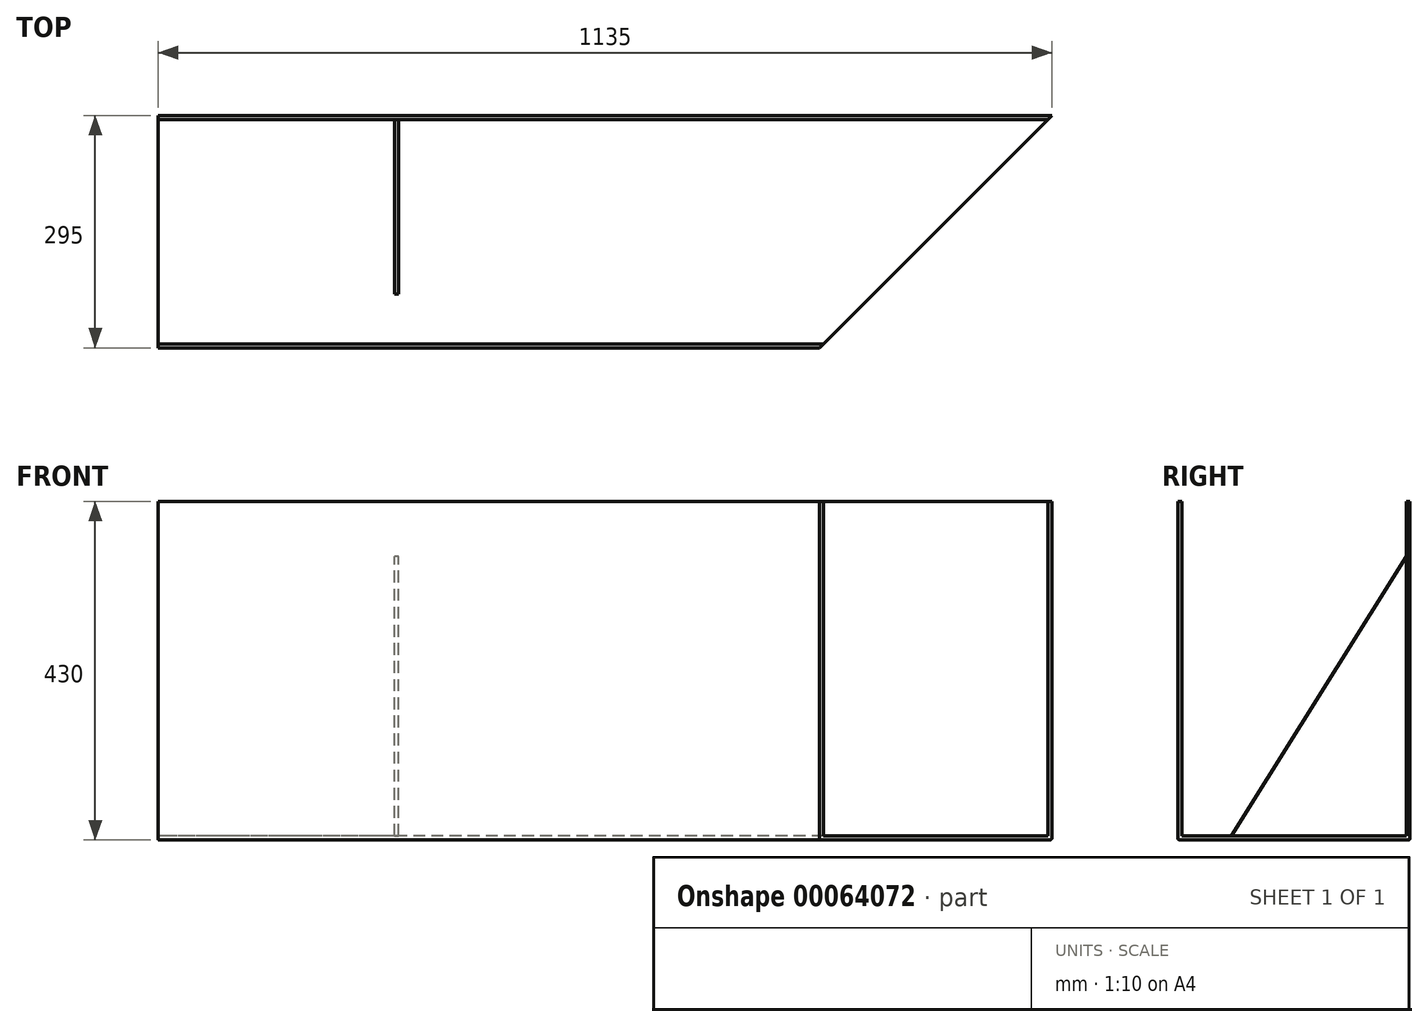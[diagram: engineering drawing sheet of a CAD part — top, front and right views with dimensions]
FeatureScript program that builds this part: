
annotation { "Feature Type Name" : "Feature", "Feature Type Description" : "" }
export const myFeature = defineFeature(function(context is Context, id is Id, definition is map)
    precondition{}
    {
        {
            var Q0;
            Q0=qCreatedBy(makeId("Right.planeOp"),FACE);
            var sketch = newSketch(context, id + "F0", { "sketchPlane" : qUnion([Q0])});
            skLineSegment(sketch, "E0.left", {"start": v(0, 0) * mm, "end": v(0, 430) * mm});
            skLineSegment(sketch, "E1", {"start": v(0, 0) * mm, "end": v(-295, 0) * mm});
            skLineSegment(sketch, "E2", {"start": v(-295, 0) * mm, "end": v(-295, 430) * mm});
            skLineSegment(sketch, "E3.0", {"start": v(-290, 5) * mm, "end": v(-290, 430) * mm});
            skLineSegment(sketch, "E3.1", {"start": v(-5, 5) * mm, "end": v(-290, 5) * mm});
            skLineSegment(sketch, "E3.2", {"start": v(-5, 5) * mm, "end": v(-5, 430) * mm});
            skLineSegment(sketch, "E4", {"start": v(0, 430) * mm, "end": v(-5, 430) * mm});
            skLineSegment(sketch, "E5", {"start": v(-290, 430) * mm, "end": v(-295, 430) * mm});
            skSolve(sketch);
        }
        {
            var Q0;
            Q0=makeQuery(id+"F0.imprint","IMPRINT",FACE,{"disambiguationData":[TD([[makeQuery(id+"F0.imprint","IMPRINT",EDGE,{"derivedFrom":sQuery(id+"F0.wireOp",EDGE,"E0.bottom")}),-1.0]])]});
            var Q1;
            Q1=makeQuery(id+"F0.imprint","IMPRINT",FACE,{"disambiguationData":[TD([[makeQuery(id+"F0.imprint","IMPRINT",EDGE,{"derivedFrom":sQuery(id+"F0.wireOp",EDGE,"E0.left")}),1.0]])]});
            extrude(context, id + "F1", {"entities" : qUnion([Q0, Q1]), "depth" : 1200 * mm});
        }
        {
            var Q0;
            Q0=qCreatedBy(makeId("Right.planeOp"),FACE);
            cPlane(context, id + "F2", {"entities" : qUnion([Q0]), "cplaneType" : CPlaneType.OFFSET, "offset" : 300 * mm, "width" : 150 * mm, "height" : 150 * mm});
        }
        {
            var Q0;
            Q0=qCreatedBy(id+"F2.planeOp",FACE);
            var sketch = newSketch(context, id + "F3", { "sketchPlane" : qUnion([Q0])});
            skLineSegment(sketch, "E6.0", {"start": v(-5, 0) * mm, "end": v(-5, 360) * mm});
            skLineSegment(sketch, "E7.0", {"start": v(-5, 0) * mm, "end": v(-230, 0) * mm});
            skPoint(sketch, "E8", {"position": v(-230, 0) * mm});
            skPoint(sketch, "E9", {"position": v(-5, 360) * mm});
            skLineSegment(sketch, "E10", {"start": v(-5, 360) * mm, "end": v(-230, 0) * mm});
            skSolve(sketch);
        }
        {
            var Q0;
            Q0=makeQuery(id+"F3.imprint","IMPRINT",FACE,{"disambiguationData":[TD([[makeQuery(id+"F3.imprint","IMPRINT",EDGE,{"derivedFrom":sQuery(id+"F3.wireOp",EDGE,"E6.0")}),1.0]])]});
            extrude(context, id + "F4", {"entities" : qUnion([Q0]), "depth" : 5 * mm});
        }
        {
            var Q0;
            Q0=qCreatedBy(makeId("Top.planeOp"),FACE);
            var sketch = newSketch(context, id + "F5", { "sketchPlane" : qUnion([Q0])});
            skLineSegment(sketch, "E11.bottom", {"start": v(0, 0) * mm, "end": v(1200, 0) * mm});
            skLineSegment(sketch, "E11.top", {"start": v(0, -230) * mm, "end": v(1200, -230) * mm});
            skLineSegment(sketch, "E11.left", {"start": v(0, 0) * mm, "end": v(0, -230) * mm});
            skLineSegment(sketch, "E11.right", {"start": v(1200, 0) * mm, "end": v(1200, -230) * mm});
            skSolve(sketch);
        }
        {
            var Q0;
            Q0=makeQuery(id+"F5.imprint","IMPRINT",FACE,{"disambiguationData":[TD([[makeQuery(id+"F5.imprint","IMPRINT",EDGE,{"derivedFrom":sQuery(id+"F5.wireOp",EDGE,"E11.bottom")}),-1.0]])]});
            extrude(context, id + "F6", {"entities" : qUnion([Q0]), "operationType" : NewBodyOperationType.ADD, "depth" : 4 * mm});
        }
        {
            var Q0;
            Q0=makeQuery(id+"F1.opExtrude","SWEPT_EDGE",EDGE,{"disambiguationData":[OSD([sQuery(id+"F0.wireOp",EDGE,"E0.left"),sQuery(id+"F0.wireOp",EDGE,"E1")])]});
            var Q1;
            Q1=makeQuery(id+"F1.opExtrude","SWEPT_EDGE",EDGE,{"disambiguationData":[OSD([sQuery(id+"F0.wireOp",EDGE,"E1"),sQuery(id+"F0.wireOp",EDGE,"E2")])]});
            fillet(context, id + "F7", {"entities" : qUnion([Q0, Q1]), "radius" : 2 * mm, "tangentPropagation" : true, "allowEdgeOverflow" : false});
        }
        {
            var Q0;
            Q0=makeQuery(id+"F1.opExtrude","SWEPT_FACE",FACE,{"disambiguationData":[OSD([sQuery(id+"F0.wireOp",EDGE,"E4")])]});
            var sketch = newSketch(context, id + "F8", { "sketchPlane" : qUnion([Q0])});
            skLineSegment(sketch, "E12.top", {"start": v(0, -295) * mm, "end": v(840, -295) * mm, "construction": true});
            skLineSegment(sketch, "E13", {"start": v(840, -295) * mm, "end": v(1135, 0) * mm});
            skLineSegment(sketch, "E14", {"start": v(840, -295) * mm, "end": v(1200, -295) * mm});
            skLineSegment(sketch, "E15", {"start": v(1200, -295) * mm, "end": v(1200, 0) * mm});
            skLineSegment(sketch, "E16", {"start": v(1200, 0) * mm, "end": v(1135, 0) * mm});
            skSolve(sketch);
        }
        {
            var Q0;
            Q0=qSketchRegion(id+"F8",true);
            extrude(context, id + "F9", {"entities" : qUnion([Q0]), "operationType" : NewBodyOperationType.REMOVE, "endBound" : BoundingType.THROUGH_ALL, "oppositeDirection" : true, "depth" : 25 * mm});
        }
    });
